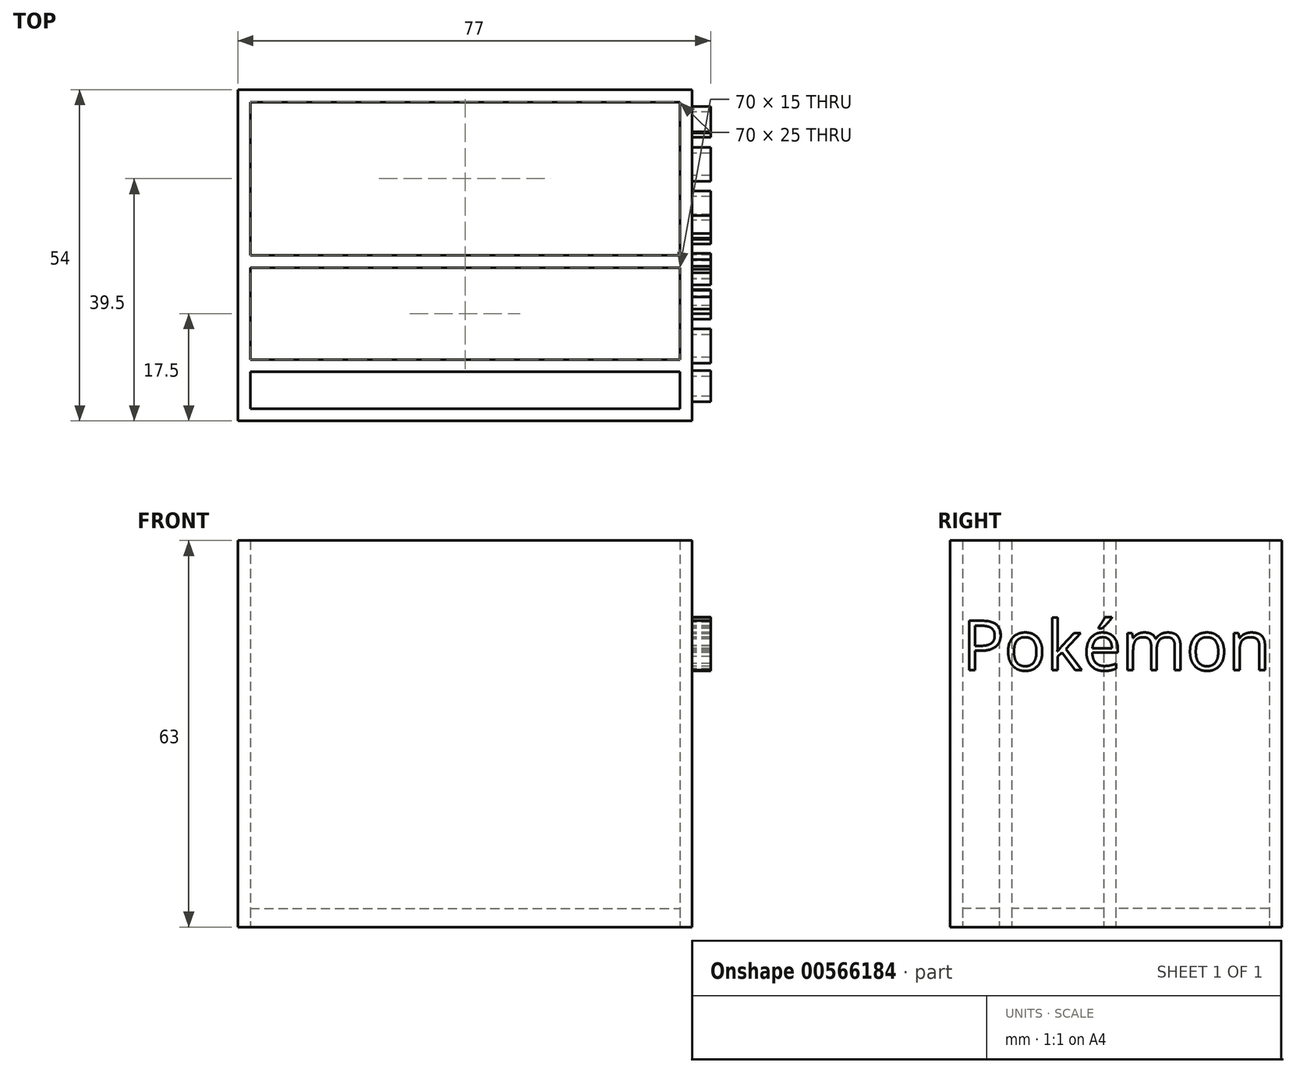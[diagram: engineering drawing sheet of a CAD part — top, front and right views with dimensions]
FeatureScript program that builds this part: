
annotation { "Feature Type Name" : "Feature", "Feature Type Description" : "" }
export const myFeature = defineFeature(function(context is Context, id is Id, definition is map)
    precondition{}
    {
        {
            var Q0;
            Q0=qCreatedBy(makeId("Top.planeOp"),FACE);
            var sketch = newSketch(context, id + "F0", { "sketchPlane" : qUnion([Q0])});
            skLineSegment(sketch, "E0.bottom", {"start": v(37, -27) * mm, "end": v(-37, -27) * mm});
            skLineSegment(sketch, "E0.top", {"start": v(37, 27) * mm, "end": v(-37, 27) * mm});
            skLineSegment(sketch, "E0.left", {"start": v(37, -27) * mm, "end": v(37, 27) * mm});
            skLineSegment(sketch, "E0.right", {"start": v(-37, -27) * mm, "end": v(-37, 27) * mm});
            skPoint(sketch, "E0.middle", {"position": v(0, 0) * mm});
            skLineSegment(sketch, "E1.bottom", {"start": v(-35, 25) * mm, "end": v(35, 25) * mm});
            skLineSegment(sketch, "E1.top", {"start": v(-35, 0) * mm, "end": v(35, 0) * mm});
            skLineSegment(sketch, "E1.left", {"start": v(-35, 25) * mm, "end": v(-35, 0) * mm});
            skLineSegment(sketch, "E1.right", {"start": v(35, 25) * mm, "end": v(35, 0) * mm});
            skLineSegment(sketch, "E2.bottom", {"start": v(-35, -2) * mm, "end": v(35, -2) * mm});
            skLineSegment(sketch, "E2.top", {"start": v(-35, -17) * mm, "end": v(35, -17) * mm});
            skLineSegment(sketch, "E2.left", {"start": v(-35, -2) * mm, "end": v(-35, -17) * mm});
            skLineSegment(sketch, "E2.right", {"start": v(35, -2) * mm, "end": v(35, -17) * mm});
            skLineSegment(sketch, "E3.bottom", {"start": v(-35, -19) * mm, "end": v(35, -19) * mm});
            skLineSegment(sketch, "E3.top", {"start": v(-35, -25) * mm, "end": v(35, -25) * mm});
            skLineSegment(sketch, "E3.left", {"start": v(-35, -19) * mm, "end": v(-35, -25) * mm});
            skLineSegment(sketch, "E3.right", {"start": v(35, -19) * mm, "end": v(35, -25) * mm});
            skSolve(sketch);
        }
        {
            var Q0;
            Q0=makeQuery(id+"F0.imprint","IMPRINT",FACE,{"disambiguationData":[TD([[makeQuery(id+"F0.imprint","IMPRINT",EDGE,{"derivedFrom":sQuery(id+"F0.wireOp",EDGE,"E1.bottom")}),-1.0]])]});
            var Q1;
            Q1=makeQuery(id+"F0.imprint","IMPRINT",FACE,{"disambiguationData":[TD([[makeQuery(id+"F0.imprint","IMPRINT",EDGE,{"derivedFrom":sQuery(id+"F0.wireOp",EDGE,"E2.bottom")}),-1.0]])]});
            var Q2;
            Q2=makeQuery(id+"F0.imprint","IMPRINT",FACE,{"disambiguationData":[TD([[makeQuery(id+"F0.imprint","IMPRINT",EDGE,{"derivedFrom":sQuery(id+"F0.wireOp",EDGE,"E3.bottom")}),-1.0]])]});
            extrude(context, id + "F1", {"entities" : qUnion([Q0, Q1, Q2]), "depth" : 3 * mm, "offsetDistance" : 25 * mm});
        }
        {
            var Q0;
            Q0=qCreatedBy(makeId("Top.planeOp"),FACE);
            var sketch = newSketch(context, id + "F2", { "sketchPlane" : qUnion([Q0])});
            skLineSegment(sketch, "E4.bottom", {"start": v(37, -27) * mm, "end": v(-37, -27) * mm});
            skLineSegment(sketch, "E4.top", {"start": v(37, 27) * mm, "end": v(-37, 27) * mm});
            skLineSegment(sketch, "E4.left", {"start": v(37, -27) * mm, "end": v(37, 27) * mm});
            skLineSegment(sketch, "E4.right", {"start": v(-37, -27) * mm, "end": v(-37, 27) * mm});
            skPoint(sketch, "E4.middle", {"position": v(0, 0) * mm});
            skLineSegment(sketch, "E5.bottom", {"start": v(-35, 25) * mm, "end": v(35, 25) * mm});
            skLineSegment(sketch, "E5.top", {"start": v(-35, 0) * mm, "end": v(35, 0) * mm});
            skLineSegment(sketch, "E5.left", {"start": v(-35, 25) * mm, "end": v(-35, 0) * mm});
            skLineSegment(sketch, "E5.right", {"start": v(35, 25) * mm, "end": v(35, 0) * mm});
            skLineSegment(sketch, "E6.bottom", {"start": v(-35, -2) * mm, "end": v(35, -2) * mm});
            skLineSegment(sketch, "E6.top", {"start": v(-35, -17) * mm, "end": v(35, -17) * mm});
            skLineSegment(sketch, "E6.left", {"start": v(-35, -2) * mm, "end": v(-35, -17) * mm});
            skLineSegment(sketch, "E6.right", {"start": v(35, -2) * mm, "end": v(35, -17) * mm});
            skLineSegment(sketch, "E7.bottom", {"start": v(-35, -19) * mm, "end": v(35, -19) * mm});
            skLineSegment(sketch, "E7.top", {"start": v(-35, -25) * mm, "end": v(35, -25) * mm});
            skLineSegment(sketch, "E7.left", {"start": v(-35, -19) * mm, "end": v(-35, -25) * mm});
            skLineSegment(sketch, "E7.right", {"start": v(35, -19) * mm, "end": v(35, -25) * mm});
            skSolve(sketch);
        }
        {
            var Q0;
            Q0=makeQuery(id+"F2.imprint","IMPRINT",FACE,{"disambiguationData":[TD([[makeQuery(id+"F2.imprint","IMPRINT",EDGE,{"derivedFrom":sQuery(id+"F2.wireOp",EDGE,"E4.bottom")}),-1.0]])]});
            extrude(context, id + "F3", {"entities" : qUnion([Q0]), "depth" : 63 * mm, "offsetDistance" : 25 * mm});
        }
        {
            var Q0;
            Q0=qCreatedBy(makeId("Right.planeOp"),FACE);
            var sketch = newSketch(context, id + "F4", { "sketchPlane" : qUnion([Q0])});
            skText(sketch, "E8", { "text": "Pokémon", "fontName": "OpenSans-Regular.ttf"});
            const initialGuessF4  = {"E8": [-0.025, 0.04186, 1, 0, 0.00814]};
            skSetInitialGuess(sketch, initialGuessF4);
            skSolve(sketch);
        }
        {
            var Q0;
            Q0 = qSketchRegion(id + "F4", true);
            extrude(context, id + "F5", {"entities" : qUnion([Q0]), "operationType" : NewBodyOperationType.ADD, "depth" : 40 * mm, "offsetDistance" : 25 * mm, "hasSecondDirection" : true, "secondDirectionOppositeDirection" : false, "secondDirectionDepth" : 37 * mm});
        }
    });
